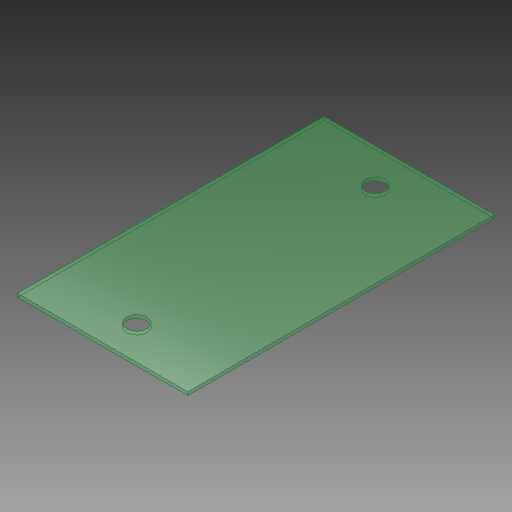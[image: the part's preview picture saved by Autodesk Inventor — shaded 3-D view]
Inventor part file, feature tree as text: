
AUTODESK INVENTOR PART (.ipt)
format: ipt  version: 2018.1 (Build 221171000, 171)  size: 108,032 bytes
history: native  units: mm
features: extrude x2, sketch x2
ambient origin geometry x8: Origin, YZ Plane, XZ Plane, XY Plane, X Axis, Y Axis, Z Axis, Center Point
bodies: Solid1 (feature_tree)
feature tree (4):
  extrude  "Extrusion1"  Depth=450.0mm
  extrude  "Extrusion2"  TaperAngle=0.0deg  [1 undecoded]
  sketch  "Sketch1"  dims[d0=250.0mm d1=450.0mm]
  sketch  "Sketch2"  dims[d2=5.0mm d3=0.0mm d4=30.0mm d5=50.0mm d6=5.0mm d7=0.0mm]
note: 1 required parameter value undecoded (feature->parameter linkage not recoverable at this tier; creation-order binding heuristic only, values carry confidence <= 0.55)
